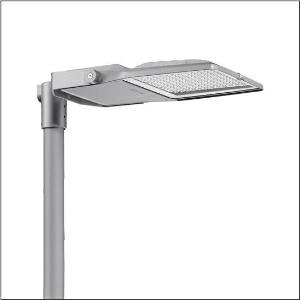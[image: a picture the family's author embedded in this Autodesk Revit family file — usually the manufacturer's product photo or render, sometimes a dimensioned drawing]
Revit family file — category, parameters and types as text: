
# Revit family: floodlight_fl_21_iq_midi___pl33t_5xa7781e6f3a_cd97
name_source: partatom
category: Lighting Fixtures
units: mm (PartAtom-declared; Revit-internal decimal feet)

## family parameters
Cut with Voids When Loaded = No
Host = Face
Light Source = No
Part Type = Normal
Room Calculation Point = No
Round Connector Dimension = Use Diameter
Shared = No

## types (1)
- --- (1 x LED, 21270 lm, 208.1 W, 5700K)
    Apparent Load = 208 VA
    CIE Flux Codes = 26 75 99 100 100
    Color Rendering = 90
    Color Temperature = 5700K
    Default Elevation = 1800 mm
    Description = Floodlight FL 21 iQ midi, floodlight, primary light control with lens, of PMMA, primary optical cover: protective disc, of toughened safety glass, transparent, light distribution: PL33T, light emission: direct distribution, installation type: surface-mounted, LED, High Power LED, rated luminous flux: 21.270lm, luminous efficacy: 102lm/W, light colour: 957, colour temperature: 5700K, control gear: ECG iQ, control: optimised constant luminous flux control (CLO 2.0), Desk-Remote (wireless, voltage-free reading and setting of iQ features in the workshop via application-optimized NFC function/RFID function), Light-Fading, Smart-Wire, Night-Set, Lumen-Switch, Temp-Guard, Auto-Match, with terminal, 6-pole, mains connection: 220..240V, AC, 50/60Hz, start of lifetime: 208W, end of service life: 227W, reduction: 90W, luminaire housing, of diecast aluminium, powder-coated, Siteco® metallic grey (DB 702S), corrosivity category C5 mid according to DIN EN ISO 12944, sealing non-destructively replaceable, please order mast flange separately, mast bracket, of steel, galvanised, powder-coated, Siteco® metallic grey (DB 702S), protection rating (complete): IP66, insulation class (complete): insulation class II (safety insulation), certification: CE, ENEC, VDE, protection symbol: D, impact resistance: IK08, permissible operating ambient temperature: -40..+40°C, permissible operating ambient temperature for outdoor applications: -40..+50°C, standard: DIN EN 12944, LABS conformity tested according to VDMA 24364:2018-05, packaging unit: 1 piece

Light Distribution: PL33T
    Height = 76 mm
    Lamp = 1 x LED
    Lamp Light Flux = 21270 lm
    Lamp Power = 208.1 W
    Lamp count = 1
    Length = 657 mm
    Luminous efficacy = 102 lm/W
    Manufacturer = Siteco
    ModVariant = No
    Model = 5XA7781E6F3A
    Number of Poles = 1
    OnlyDefault = Yes
    Power Factor = 1
    Product Name = Floodlight FL 21 iQ midi | PL33T
    Product group = floodlight | pylon annexe
    ProductGroupID = 6200
    Protection Class = Protection class II
    Protection Degree = IP 66
    RLX_Detail_Level = 1
    RLX_Emergency_Light_Flux = 0 lm
    RLX_Emergency_Type = 0
    RLX_Emergency_Type_DB = No
    RlxData = <blob elided: 153721 chars, md5=2b245d80>
    Socket = socket
    Standby Power = 0 W
    System Light Flux = 21270 lm
    System Power = 208 W
    Type Comments = factory setting: luminous flux: 100 % | dim-lin: 254 | 710 mA
    Type Image = l_1007123.jpg
    URL = http://relux.com
    VarID = @adj_072487
    Voltage = 0 V
    Weight = 0.00 kg
    Width = 442 mm

## geometry (parser evidence)
native form markers: Blend x4, Sweep x15
no freeform markers — native parametric forms only
